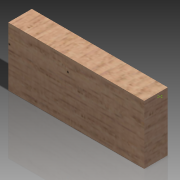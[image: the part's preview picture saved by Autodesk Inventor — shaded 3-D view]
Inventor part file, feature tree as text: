
AUTODESK INVENTOR PART (.ipt)
format: ipt  version: 2014 SP1 (Build 180222100, 222)  size: 128,000 bytes
history: native  units: mm
features: sketch x3, extrude x1
ambient origin geometry x8: Origin, YZ Plane, XZ Plane, XY Plane, X Axis, Y Axis, Z Axis, Center Point
bodies: Volumenkörper1 (feature_tree)
feature tree (4):
  extrude  "Extrusion1"  Depth=45.0mm
  sketch  "Skizze1"  dims[d0=104.0mm d1=45.0mm]
  sketch  "Skizze2"  dims[d2=18.0mm d3=0.0mm]
  sketch  "Skizze3"
